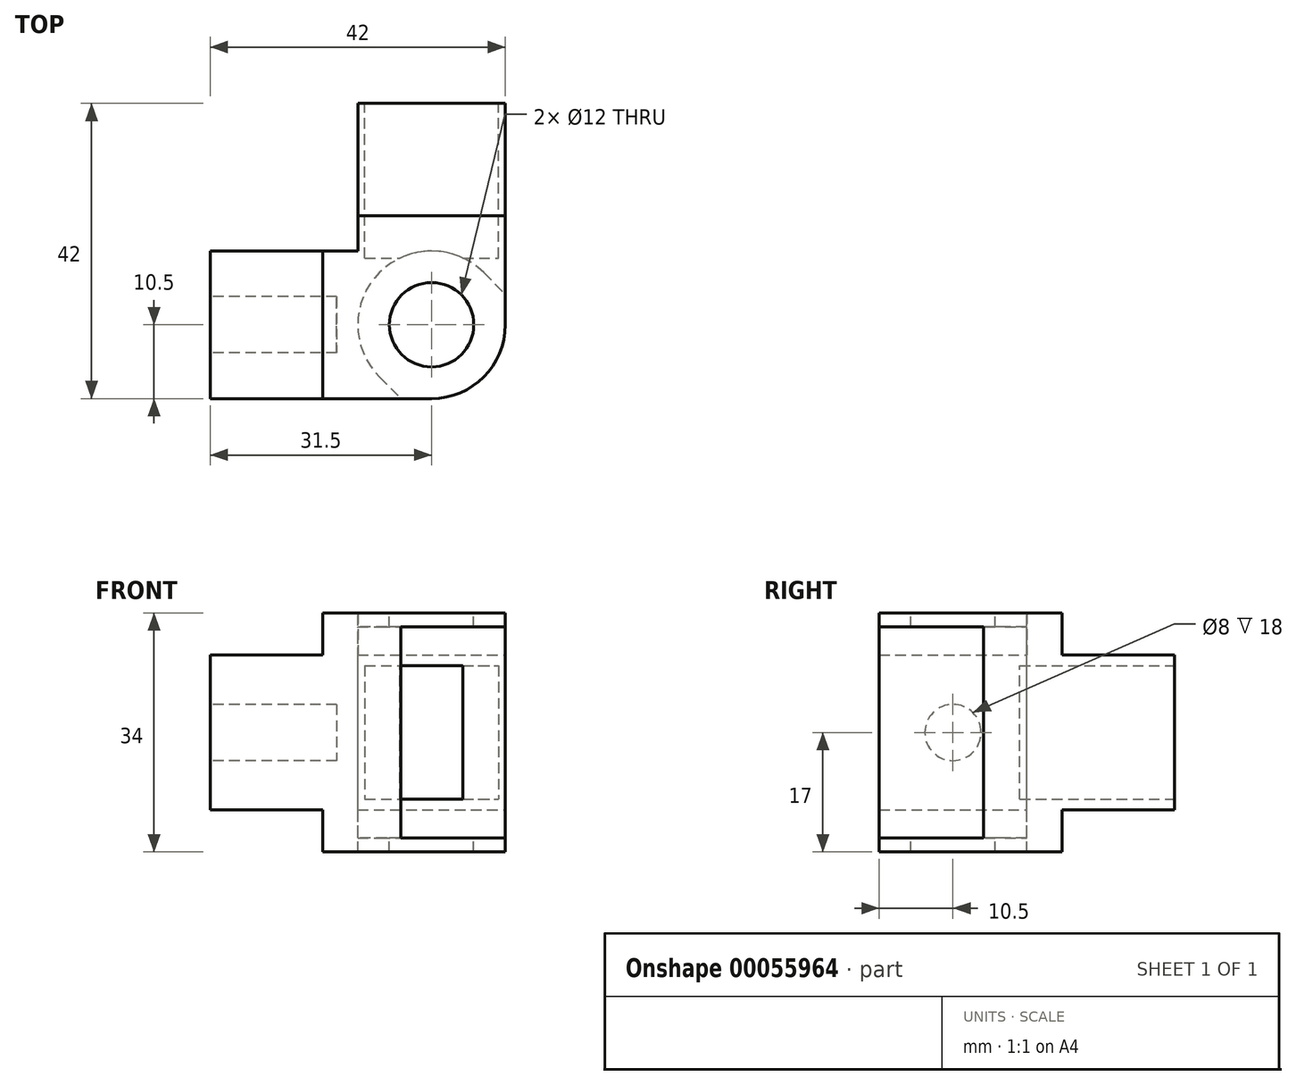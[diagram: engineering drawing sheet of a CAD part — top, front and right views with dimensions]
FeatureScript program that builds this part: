
annotation { "Feature Type Name" : "Feature", "Feature Type Description" : "" }
export const myFeature = defineFeature(function(context is Context, id is Id, definition is map)
    precondition{}
    {
        {
            var Q0;
            Q0=qCreatedBy(makeId("Top.planeOp"),FACE);
            var sketch = newSketch(context, id + "F0", { "sketchPlane" : qUnion([Q0])});
            skLineSegment(sketch, "E0.rect.bottom", {"start": v(21, -21) * mm, "end": v(-21, -21) * mm});
            skLineSegment(sketch, "E0.rect.top", {"start": v(21, 21) * mm, "end": v(-21, 21) * mm});
            skLineSegment(sketch, "E0.rect.left", {"start": v(21, -21) * mm, "end": v(21, 21) * mm});
            skLineSegment(sketch, "E0.rect.right", {"start": v(-21, -21) * mm, "end": v(-21, 21) * mm});
            skPoint(sketch, "E0.rect.middle", {"position": v(0, 0) * mm});
            skSolve(sketch);
        }
        {
            var Q0;
            Q0=makeQuery(id+"F0.imprint","IMPRINT",FACE,{"disambiguationData":[TD([[makeQuery(id+"F0.imprint","IMPRINT",EDGE,{"derivedFrom":sQuery(id+"F0.wireOp",EDGE,"E0.rect.bottom")}),-1.0]])]});
            extrude(context, id + "F1", {"entities" : qUnion([Q0]), "depth" : 22 * mm});
        }
        {
            var Q0;
            Q0=makeQuery(id+"F1.opExtrude","CAP_FACE",FACE,{"disambiguationData":[OSD([sQuery(id+"F0.wireOp",EDGE,"E0.rect.bottom"),sQuery(id+"F0.wireOp",EDGE,"E0.rect.top"),sQuery(id+"F0.wireOp",EDGE,"E0.rect.left"),sQuery(id+"F0.wireOp",EDGE,"E0.rect.right")])],"isStart":false});
            var sketch = newSketch(context, id + "F2", { "sketchPlane" : qUnion([Q0])});
            skLineSegment(sketch, "E1.bottom", {"start": v(-21, 21) * mm, "end": v(0, 21) * mm});
            skLineSegment(sketch, "E1.top", {"start": v(-21, 0) * mm, "end": v(0, 0) * mm});
            skLineSegment(sketch, "E1.left", {"start": v(-21, 21) * mm, "end": v(-21, 0) * mm});
            skLineSegment(sketch, "E1.right", {"start": v(0, 21) * mm, "end": v(0, 0) * mm});
            skSolve(sketch);
        }
        {
            var Q0;
            Q0=makeQuery(id+"F2.imprint","IMPRINT",FACE,{"disambiguationData":[TD([[makeQuery(id+"F2.imprint","IMPRINT",EDGE,{"derivedFrom":sQuery(id+"F2.wireOp",EDGE,"E1.bottom")}),1.0]])]});
            extrude(context, id + "F3", {"entities" : qUnion([Q0]), "operationType" : NewBodyOperationType.REMOVE, "endBound" : BoundingType.UP_TO_NEXT, "oppositeDirection" : true, "depth" : 25 * mm});
        }
        {
            var Q0;
            Q0=makeQuery(id+"F1.opExtrude","CAP_FACE",FACE,{"disambiguationData":[OSD([sQuery(id+"F0.wireOp",EDGE,"E0.rect.bottom"),sQuery(id+"F0.wireOp",EDGE,"E0.rect.top"),sQuery(id+"F0.wireOp",EDGE,"E0.rect.left"),sQuery(id+"F0.wireOp",EDGE,"E0.rect.right")])],"isStart":false});
            var sketch = newSketch(context, id + "F4", { "sketchPlane" : qUnion([Q0])});
            skLineSegment(sketch, "E2", {"start": v(0, 0) * mm, "end": v(21, -21) * mm, "construction": true});
            skCircle(sketch, "E3", {"center": v(10.5, -10.5) * mm, "radius": 6 * mm});
            skSolve(sketch);
        }
        {
            var Q0;
            Q0=makeQuery(id+"F4.imprint","IMPRINT",FACE,{"disambiguationData":[TD([[makeQuery(id+"F4.imprint","IMPRINT",EDGE,{"derivedFrom":sQuery(id+"F4.wireOp",EDGE,"E3")}),1.0]])]});
            var Q1;
            Q1=makeQuery(id+"F1.opExtrude","CAP_FACE",FACE,{"disambiguationData":[OSD([sQuery(id+"F0.wireOp",EDGE,"E0.rect.bottom"),sQuery(id+"F0.wireOp",EDGE,"E0.rect.top"),sQuery(id+"F0.wireOp",EDGE,"E0.rect.left"),sQuery(id+"F0.wireOp",EDGE,"E0.rect.right")])],"isStart":true});
            extrude(context, id + "F5", {"entities" : qUnion([Q0]), "operationType" : NewBodyOperationType.REMOVE, "endBound" : BoundingType.UP_TO_SURFACE, "oppositeDirection" : true, "endBoundEntityFace" : qUnion([Q1]), "depth" : 25 * mm});
        }
        {
            var Q0;
            Q0=makeQuery(id+"F1.opExtrude","SWEPT_FACE",FACE,{"disambiguationData":[OSD([sQuery(id+"F0.wireOp",EDGE,"E0.rect.right")])]});
            var sketch = newSketch(context, id + "F6", { "sketchPlane" : qUnion([Q0])});
            skLineSegment(sketch, "E4", {"start": v(0, 22) * mm, "end": v(21, 0) * mm, "construction": true});
            skCircle(sketch, "E5", {"center": v(10.5, 11) * mm, "radius": 4 * mm});
            skSolve(sketch);
        }
        {
            var Q0;
            Q0=makeQuery(id+"F6.imprint","IMPRINT",FACE,{"disambiguationData":[TD([[makeQuery(id+"F6.imprint","IMPRINT",EDGE,{"derivedFrom":sQuery(id+"F6.wireOp",EDGE,"E5")}),1.0]])]});
            extrude(context, id + "F7", {"entities" : qUnion([Q0]), "operationType" : NewBodyOperationType.REMOVE, "oppositeDirection" : true, "depth" : 18 * mm});
        }
        {
            var Q0;
            Q0=makeQuery(id+"F1.opExtrude","SWEPT_FACE",FACE,{"disambiguationData":[OSD([sQuery(id+"F0.wireOp",EDGE,"E0.rect.top")])]});
            var sketch = newSketch(context, id + "F8", { "sketchPlane" : qUnion([Q0])});
            skLineSegment(sketch, "E6", {"start": v(-21, 22) * mm, "end": v(0, 0) * mm, "construction": true});
            skLineSegment(sketch, "E7.rect.bottom", {"start": v(-1, 20.5) * mm, "end": v(-20, 20.5) * mm});
            skLineSegment(sketch, "E7.rect.top", {"start": v(-1, 1.5) * mm, "end": v(-20, 1.5) * mm});
            skLineSegment(sketch, "E7.rect.left", {"start": v(-1, 20.5) * mm, "end": v(-1, 1.5) * mm});
            skLineSegment(sketch, "E7.rect.right", {"start": v(-20, 20.5) * mm, "end": v(-20, 1.5) * mm});
            skPoint(sketch, "E7.rect.middle", {"position": v(-10.5, 11) * mm});
            skSolve(sketch);
        }
        {
            var Q0;
            Q0=makeQuery(id+"F8.imprint","IMPRINT",FACE,{"disambiguationData":[TD([[makeQuery(id+"F8.imprint","IMPRINT",EDGE,{"derivedFrom":sQuery(id+"F8.wireOp",EDGE,"E7.rect.bottom")}),1.0]])]});
            extrude(context, id + "F9", {"entities" : qUnion([Q0]), "operationType" : NewBodyOperationType.REMOVE, "oppositeDirection" : true, "depth" : 22 * mm});
        }
        {
            var Q0;
            Q0=makeQuery(id+"F1.opExtrude","CAP_FACE",FACE,{"disambiguationData":[OSD([sQuery(id+"F0.wireOp",EDGE,"E0.rect.bottom"),sQuery(id+"F0.wireOp",EDGE,"E0.rect.top"),sQuery(id+"F0.wireOp",EDGE,"E0.rect.left"),sQuery(id+"F0.wireOp",EDGE,"E0.rect.right")])],"isStart":false});
            var sketch = newSketch(context, id + "F10", { "sketchPlane" : qUnion([Q0])});
            skLineSegment(sketch, "E8.bottom", {"start": v(0, 0) * mm, "end": v(21, 0) * mm});
            skLineSegment(sketch, "E8.top", {"start": v(0, -21) * mm, "end": v(21, -21) * mm});
            skLineSegment(sketch, "E8.left", {"start": v(0, 0) * mm, "end": v(0, -21) * mm});
            skLineSegment(sketch, "E8.right", {"start": v(21, 0) * mm, "end": v(21, -21) * mm});
            skLineSegment(sketch, "E9.top", {"start": v(0, 5) * mm, "end": v(21, 5) * mm});
            skLineSegment(sketch, "E9.left", {"start": v(0, 0) * mm, "end": v(0, 5) * mm});
            skLineSegment(sketch, "E9.right", {"start": v(21, 0) * mm, "end": v(21, 5) * mm});
            skLineSegment(sketch, "E10.bottom", {"start": v(0, 0) * mm, "end": v(-5, 0) * mm});
            skLineSegment(sketch, "E10.top", {"start": v(0, -21) * mm, "end": v(-5, -21) * mm});
            skLineSegment(sketch, "E10.right", {"start": v(-5, 0) * mm, "end": v(-5, -21) * mm});
            skSolve(sketch);
        }
        {
            var Q0;
            Q0=makeQuery(id+"F10.imprint","IMPRINT",FACE,{"disambiguationData":[TD([[makeQuery(id+"F10.imprint","IMPRINT",EDGE,{"derivedFrom":sQuery(id+"F10.wireOp",EDGE,"E8.bottom")}),-1.0]])]});
            var Q1;
            Q1=makeQuery(id+"F10.imprint","IMPRINT",FACE,{"disambiguationData":[TD([[makeQuery(id+"F10.imprint","IMPRINT",EDGE,{"derivedFrom":sQuery(id+"F10.wireOp",EDGE,"E8.bottom")}),1.0]])]});
            var Q2;
            Q2=makeQuery(id+"F10.imprint","IMPRINT",FACE,{"disambiguationData":[TD([[makeQuery(id+"F10.imprint","IMPRINT",EDGE,{"derivedFrom":sQuery(id+"F10.wireOp",EDGE,"E10.bottom")}),-1.0]])]});
            var Q3;
            Q3=makeQuery(id+"F10.imprint","IMPRINT",FACE,{"disambiguationData":[TD([[makeQuery(id+"F10.imprint","IMPRINT",EDGE,{"derivedFrom":sQuery(id+"F10.wireOp",EDGE,"E8.top")}),-1.0]])]});
            extrude(context, id + "F11", {"entities" : qUnion([Q0, Q1, Q2, Q3]), "operationType" : NewBodyOperationType.ADD, "depth" : 6 * mm});
        }
        {
            var Q0;
            Q0=makeQuery(id+"F1.opExtrude","CAP_FACE",FACE,{"disambiguationData":[OSD([sQuery(id+"F0.wireOp",EDGE,"E0.rect.bottom"),sQuery(id+"F0.wireOp",EDGE,"E0.rect.top"),sQuery(id+"F0.wireOp",EDGE,"E0.rect.left"),sQuery(id+"F0.wireOp",EDGE,"E0.rect.right")])],"isStart":true});
            var sketch = newSketch(context, id + "F12", { "sketchPlane" : qUnion([Q0])});
            skLineSegment(sketch, "E11.bottom", {"start": v(0, 0) * mm, "end": v(21, 0) * mm});
            skLineSegment(sketch, "E11.top", {"start": v(0, 21) * mm, "end": v(21, 21) * mm});
            skLineSegment(sketch, "E11.left", {"start": v(0, 0) * mm, "end": v(0, 21) * mm});
            skLineSegment(sketch, "E11.right", {"start": v(21, 0) * mm, "end": v(21, 21) * mm});
            skLineSegment(sketch, "E12.bottom", {"start": v(0, 0) * mm, "end": v(-5, 0) * mm});
            skLineSegment(sketch, "E12.top", {"start": v(0, 21) * mm, "end": v(-5, 21) * mm});
            skLineSegment(sketch, "E12.right", {"start": v(-5, 0) * mm, "end": v(-5, 21) * mm});
            skLineSegment(sketch, "E13.top", {"start": v(0, -5) * mm, "end": v(21, -5) * mm});
            skLineSegment(sketch, "E13.left", {"start": v(0, 0) * mm, "end": v(0, -5) * mm});
            skLineSegment(sketch, "E13.right", {"start": v(21, 0) * mm, "end": v(21, -5) * mm});
            skSolve(sketch);
        }
        {
            var Q0;
            Q0=makeQuery(id+"F12.imprint","IMPRINT",FACE,{"disambiguationData":[TD([[makeQuery(id+"F12.imprint","IMPRINT",EDGE,{"derivedFrom":sQuery(id+"F12.wireOp",EDGE,"E11.top")}),1.0]])]});
            var Q1;
            Q1=makeQuery(id+"F12.imprint","IMPRINT",FACE,{"disambiguationData":[TD([[makeQuery(id+"F12.imprint","IMPRINT",EDGE,{"derivedFrom":sQuery(id+"F12.wireOp",EDGE,"E12.bottom")}),-1.0]])]});
            var Q2;
            Q2=makeQuery(id+"F12.imprint","IMPRINT",FACE,{"disambiguationData":[TD([[makeQuery(id+"F12.imprint","IMPRINT",EDGE,{"derivedFrom":sQuery(id+"F12.wireOp",EDGE,"E11.bottom")}),-1.0]])]});
            extrude(context, id + "F13", {"entities" : qUnion([Q0, Q1, Q2]), "operationType" : NewBodyOperationType.ADD, "depth" : 6 * mm});
        }
        {
            var Q0;
            {var subQ0=sQuery(id+"F0.wireOp",EDGE,"E0.rect.right");var subQ1=sQuery(id+"F0.wireOp",EDGE,"E0.rect.bottom");Q0=makeQuery(id+"F11.boolean.opBoolean","SPLIT",FACE,{"disambiguationData":[TD([makeQuery(id+"F1.opExtrude","SWEPT_FACE",FACE,{"disambiguationData":[OSD([subQ1])]})])],"derivedFrom":makeQuery(id+"F1.opExtrude","CAP_FACE",FACE,{"disambiguationData":[OSD([subQ1,sQuery(id+"F0.wireOp",EDGE,"E0.rect.top"),sQuery(id+"F0.wireOp",EDGE,"E0.rect.left"),subQ0])],"isStart":false})});}
            cPlane(context, id + "F14", {"entities" : qUnion([Q0]), "cplaneType" : CPlaneType.OFFSET, "offset" : 11 * mm, "oppositeDirection" : true, "width" : 150 * mm, "height" : 150 * mm});
        }
        {
            var Q0;
            Q0=qCreatedBy(id+"F14.planeOp",FACE);
            var sketch = newSketch(context, id + "F15", { "sketchPlane" : qUnion([Q0])});
            skCircle(sketch, "E14.0", {"center": v(10.5, -10.5) * mm, "radius": 6 * mm});
            skCircle(sketch, "E15", {"center": v(10.5, -10.5) * mm, "radius": 10.5 * mm});
            skLineSegment(sketch, "E16", {"start": v(0, -10.5) * mm, "end": v(21, -10.5) * mm, "construction": true});
            skLineSegment(sketch, "E17", {"start": v(10.5, 0) * mm, "end": v(10.5, -21) * mm, "construction": true});
            skLineSegment(sketch, "E18.bottom", {"start": v(0, -10.5) * mm, "end": v(10.5, -10.5) * mm, "construction": true});
            skLineSegment(sketch, "E18.top", {"start": v(0, 0) * mm, "end": v(10.5, 0) * mm, "construction": true});
            skLineSegment(sketch, "E18.left", {"start": v(0, -10.5) * mm, "end": v(0, 0) * mm, "construction": true});
            skLineSegment(sketch, "E18.right", {"start": v(10.5, -10.5) * mm, "end": v(10.5, 0) * mm, "construction": true});
            skLineSegment(sketch, "E19", {"start": v(0, 0) * mm, "end": v(10.5, -10.5) * mm, "construction": true});
            skLineSegment(sketch, "E20.bottom", {"start": v(21, -10.5) * mm, "end": v(10.5, -10.5) * mm, "construction": true});
            skLineSegment(sketch, "E20.top", {"start": v(21, -21) * mm, "end": v(10.5, -21) * mm, "construction": true});
            skLineSegment(sketch, "E20.left", {"start": v(21, -10.5) * mm, "end": v(21, -21) * mm, "construction": true});
            skLineSegment(sketch, "E20.right", {"start": v(10.5, -10.5) * mm, "end": v(10.5, -21) * mm, "construction": true});
            skLineSegment(sketch, "E21", {"start": v(10.5, -10.5) * mm, "end": v(17.92, -17.92) * mm, "construction": true});
            skLineSegment(sketch, "E22.bottom", {"start": v(17.92, -17.92) * mm, "end": v(3.08, -17.92) * mm, "construction": true});
            skLineSegment(sketch, "E22.top", {"start": v(17.92, -3.08) * mm, "end": v(3.08, -3.08) * mm, "construction": true});
            skLineSegment(sketch, "E22.left", {"start": v(17.92, -17.92) * mm, "end": v(17.92, -3.08) * mm, "construction": true});
            skLineSegment(sketch, "E22.right", {"start": v(3.08, -17.92) * mm, "end": v(3.08, -3.08) * mm, "construction": true});
            skLineSegment(sketch, "E23.bottom", {"start": v(3.08, -17.92) * mm, "end": v(6.15, -17.92) * mm, "construction": true});
            skLineSegment(sketch, "E23.top", {"start": v(3.08, -21) * mm, "end": v(6.15, -21) * mm, "construction": true});
            skLineSegment(sketch, "E23.left", {"start": v(3.08, -17.92) * mm, "end": v(3.08, -21) * mm, "construction": true});
            skLineSegment(sketch, "E23.right", {"start": v(6.15, -17.92) * mm, "end": v(6.15, -21) * mm, "construction": true});
            skLineSegment(sketch, "E24.bottom", {"start": v(17.92, -3.08) * mm, "end": v(21, -3.08) * mm, "construction": true});
            skLineSegment(sketch, "E24.top", {"start": v(17.92, -6.15) * mm, "end": v(21, -6.15) * mm, "construction": true});
            skLineSegment(sketch, "E24.left", {"start": v(17.92, -3.08) * mm, "end": v(17.92, -6.15) * mm, "construction": true});
            skLineSegment(sketch, "E24.right", {"start": v(21, -3.08) * mm, "end": v(21, -6.15) * mm, "construction": true});
            skLineSegment(sketch, "E25", {"start": v(3.08, -17.92) * mm, "end": v(6.15, -21) * mm});
            skLineSegment(sketch, "E26", {"start": v(17.92, -3.08) * mm, "end": v(21, -6.15) * mm});
            skLineSegment(sketch, "E27", {"start": v(21, -6.15) * mm, "end": v(21, -21) * mm});
            skLineSegment(sketch, "E28", {"start": v(6.15, -21) * mm, "end": v(21, -21) * mm});
            skSolve(sketch);
        }
        {
            var Q0;
            {var subQ0=sQuery(id+"F15.wireOp",EDGE,"E27");var subQ1=sQuery(id+"F15.wireOp",EDGE,"E15");var subQ2=makeQuery(id+"F15.imprint","INTERSECT",VERTEX,{"derivedFrom":[subQ1,subQ0]});Q0=makeQuery(id+"F15.imprint","IMPRINT",FACE,{"disambiguationData":[TD([[makeQuery(id+"F15.imprint","IMPRINT",EDGE,{"disambiguationData":[TD([[subQ2,1.0]])],"derivedFrom":subQ1}),-1.0]])]});}
            var Q1;
            {var subQ0=sQuery(id+"F15.wireOp",EDGE,"E25");Q1=makeQuery(id+"F15.imprint","IMPRINT",FACE,{"disambiguationData":[TD([[makeQuery(id+"F15.imprint","IMPRINT",EDGE,{"derivedFrom":subQ0}),1.0]])]});}
            var Q2;
            {var subQ0=sQuery(id+"F15.wireOp",EDGE,"E26");Q2=makeQuery(id+"F15.imprint","IMPRINT",FACE,{"disambiguationData":[TD([[makeQuery(id+"F15.imprint","IMPRINT",EDGE,{"derivedFrom":subQ0}),-1.0]])]});}
            var Q3;
            Q3=makeQuery(id+"F15.imprint","IMPRINT",FACE,{"disambiguationData":[TD([[makeQuery(id+"F15.imprint","IMPRINT",EDGE,{"derivedFrom":sQuery(id+"F15.wireOp",EDGE,"E14.0")}),-1.0]])]});
            extrude(context, id + "F16", {"entities" : qUnion([Q0, Q1, Q2, Q3]), "operationType" : NewBodyOperationType.REMOVE, "oppositeDirection" : true, "depth" : 30 * mm, "symmetric" : true});
        }
        {
            var Q0;
            Q0=makeQuery(id+"F11.opExtrude","CAP_FACE",FACE,{"disambiguationData":[OSD([sQuery(id+"F4.wireOp",EDGE,"E3"),sQuery(id+"F10.wireOp",EDGE,"E8.top"),sQuery(id+"F10.wireOp",EDGE,"E8.right"),sQuery(id+"F10.wireOp",EDGE,"E9.top"),sQuery(id+"F10.wireOp",EDGE,"E9.left"),sQuery(id+"F10.wireOp",EDGE,"E9.right"),sQuery(id+"F10.wireOp",EDGE,"E10.bottom"),sQuery(id+"F10.wireOp",EDGE,"E10.top"),sQuery(id+"F10.wireOp",EDGE,"E10.right")])],"isStart":false});
            var sketch = newSketch(context, id + "F17", { "sketchPlane" : qUnion([Q0])});
            skCircle(sketch, "E29", {"center": v(10.5, -10.5) * mm, "radius": 10.5 * mm});
            skSolve(sketch);
        }
        {
            var Q0;
            {var subQ0=sQuery(id+"F17.wireOp",EDGE,"E29");var subQ1=makeQuery(id+"F11.opExtrude","CAP_EDGE",EDGE,{"disambiguationData":[OSD([sQuery(id+"F10.wireOp",EDGE,"E8.top"),sQuery(id+"F10.wireOp",EDGE,"E10.top")])],"isStart":false});var subQ2=makeQuery(id+"F17.imprint","INTERSECT",VERTEX,{"derivedFrom":[subQ1,subQ0]});Q0=makeQuery(id+"F17.imprint","IMPRINT",FACE,{"disambiguationData":[TD([[makeQuery(id+"F17.imprint","IMPRINT",EDGE,{"disambiguationData":[TD([[subQ2,-1.0]])],"derivedFrom":subQ0}),-1.0]])]});}
            extrude(context, id + "F18", {"entities" : qUnion([Q0]), "operationType" : NewBodyOperationType.REMOVE, "endBound" : BoundingType.THROUGH_ALL, "oppositeDirection" : true, "depth" : 25 * mm});
        }
    });
